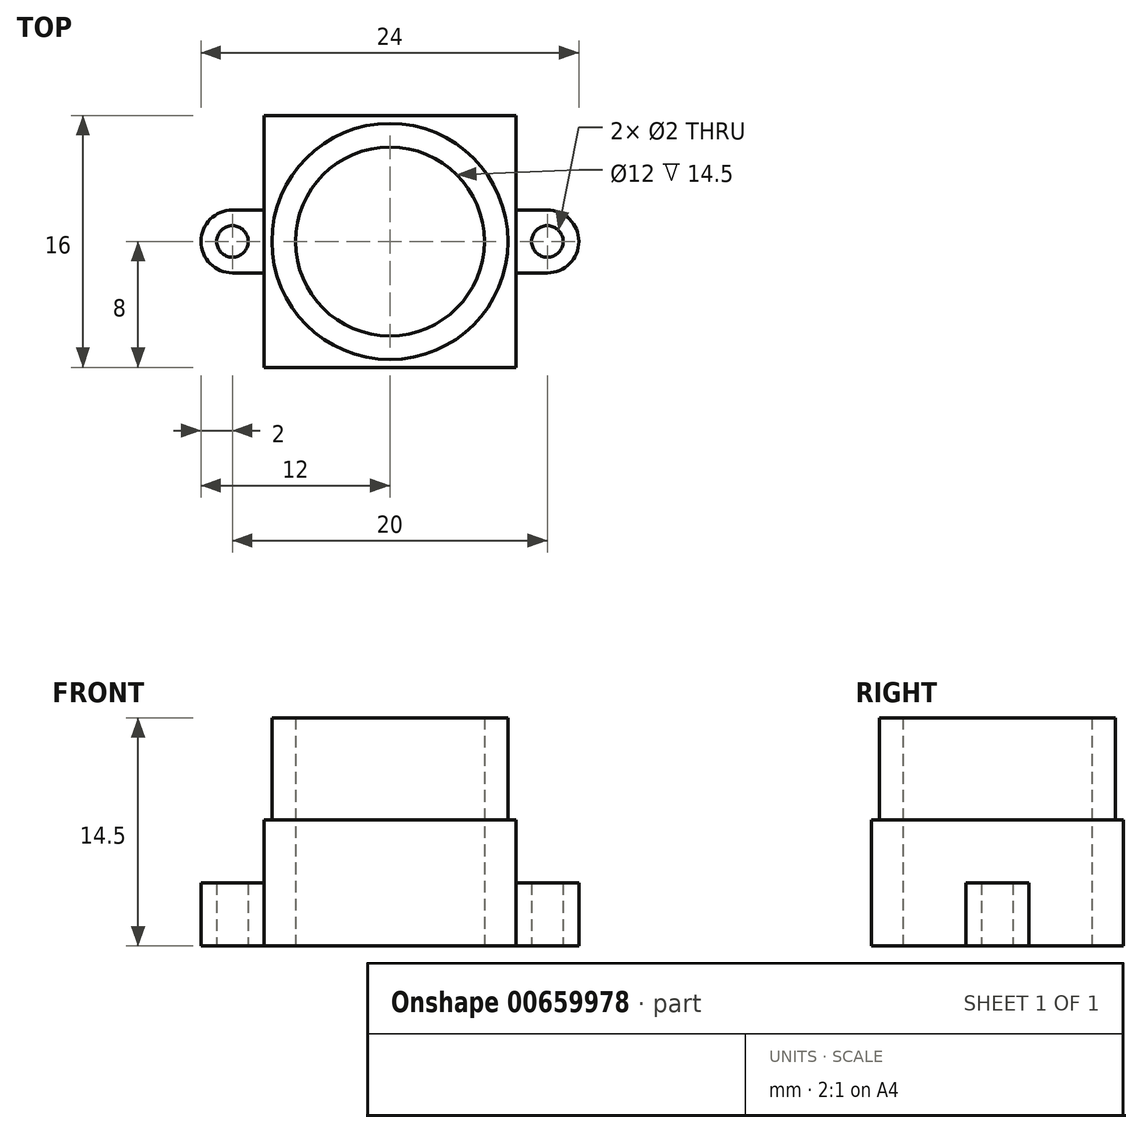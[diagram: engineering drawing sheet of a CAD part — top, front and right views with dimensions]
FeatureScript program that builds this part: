
annotation { "Feature Type Name" : "Feature", "Feature Type Description" : "" }
export const myFeature = defineFeature(function(context is Context, id is Id, definition is map)
    precondition{}
    {
        {
            var Q0;
            Q0=qCreatedBy(makeId("Top.planeOp"),FACE);
            var sketch = newSketch(context, id + "F0", { "sketchPlane" : qUnion([Q0])});
            skCircle(sketch, "E0", {"center": v(0, 0) * mm, "radius": 6 * mm});
            skLineSegment(sketch, "E1.bottom", {"start": v(8, 8) * mm, "end": v(-8, 8) * mm});
            skLineSegment(sketch, "E1.top", {"start": v(8, -8) * mm, "end": v(-8, -8) * mm});
            skLineSegment(sketch, "E1.left", {"start": v(8, 8) * mm, "end": v(8, -8) * mm});
            skLineSegment(sketch, "E1.right", {"start": v(-8, 8) * mm, "end": v(-8, -8) * mm});
            skCircle(sketch, "E2", {"center": v(-10, 0) * mm, "radius": 1 * mm});
            skCircle(sketch, "E3", {"center": v(10, 0) * mm, "radius": 1 * mm});
            skLineSegment(sketch, "E4", {"start": v(0, 0) * mm, "end": v(10, 0) * mm, "construction": true});
            skLineSegment(sketch, "E5", {"start": v(0, 0) * mm, "end": v(-10, 0) * mm, "construction": true});
            skArc(sketch, "E6", {"start": v(-10, 2) * mm, "mid": v(-12, 0) * mm, "end": v(-10, -2) * mm});
            skArc(sketch, "E7", {"start": v(10, -2) * mm, "mid": v(12, 0) * mm, "end": v(10, 2) * mm});
            skLineSegment(sketch, "E8", {"start": v(-10, 2) * mm, "end": v(-8, 2) * mm});
            skLineSegment(sketch, "E9", {"start": v(-10, -2) * mm, "end": v(-8, -2) * mm});
            skLineSegment(sketch, "E10", {"start": v(10, -2) * mm, "end": v(8, -2) * mm});
            skLineSegment(sketch, "E11", {"start": v(10, 2) * mm, "end": v(8, 2) * mm});
            skCircle(sketch, "E12", {"center": v(0, 0) * mm, "radius": 7.5 * mm});
            skSolve(sketch);
        }
        {
            var Q0;
            Q0=makeQuery(id+"F0.imprint","IMPRINT",FACE,{"disambiguationData":[TD([[makeQuery(id+"F0.imprint","IMPRINT",EDGE,{"derivedFrom":sQuery(id+"F0.wireOp",EDGE,"E0")}),-1.0]])]});
            extrude(context, id + "F1", {"entities" : qUnion([Q0]), "depth" : 14.5 * mm, "offsetDistance" : 25 * mm});
        }
        {
            var Q0;
            {var subQ3=sQuery(id+"F0.wireOp",EDGE,"E1.bottom");Q0=makeQuery(id+"F0.imprint","IMPRINT",FACE,{"disambiguationData":[TD([[makeQuery(id+"F0.imprint","IMPRINT",EDGE,{"derivedFrom":subQ3}),1.0]])]});}
            extrude(context, id + "F2", {"entities" : qUnion([Q0]), "operationType" : NewBodyOperationType.ADD, "depth" : 8 * mm, "offsetDistance" : 25 * mm});
        }
        {
            var Q0;
            Q0=makeQuery(id+"F0.imprint","IMPRINT",FACE,{"disambiguationData":[TD([[makeQuery(id+"F0.imprint","IMPRINT",EDGE,{"derivedFrom":sQuery(id+"F0.wireOp",EDGE,"E2")}),-1.0]])]});
            var Q1;
            Q1=makeQuery(id+"F0.imprint","IMPRINT",FACE,{"disambiguationData":[TD([[makeQuery(id+"F0.imprint","IMPRINT",EDGE,{"derivedFrom":sQuery(id+"F0.wireOp",EDGE,"E3")}),-1.0]])]});
            extrude(context, id + "F3", {"entities" : qUnion([Q0, Q1]), "operationType" : NewBodyOperationType.ADD, "depth" : 4 * mm, "offsetDistance" : 25 * mm});
        }
    });
